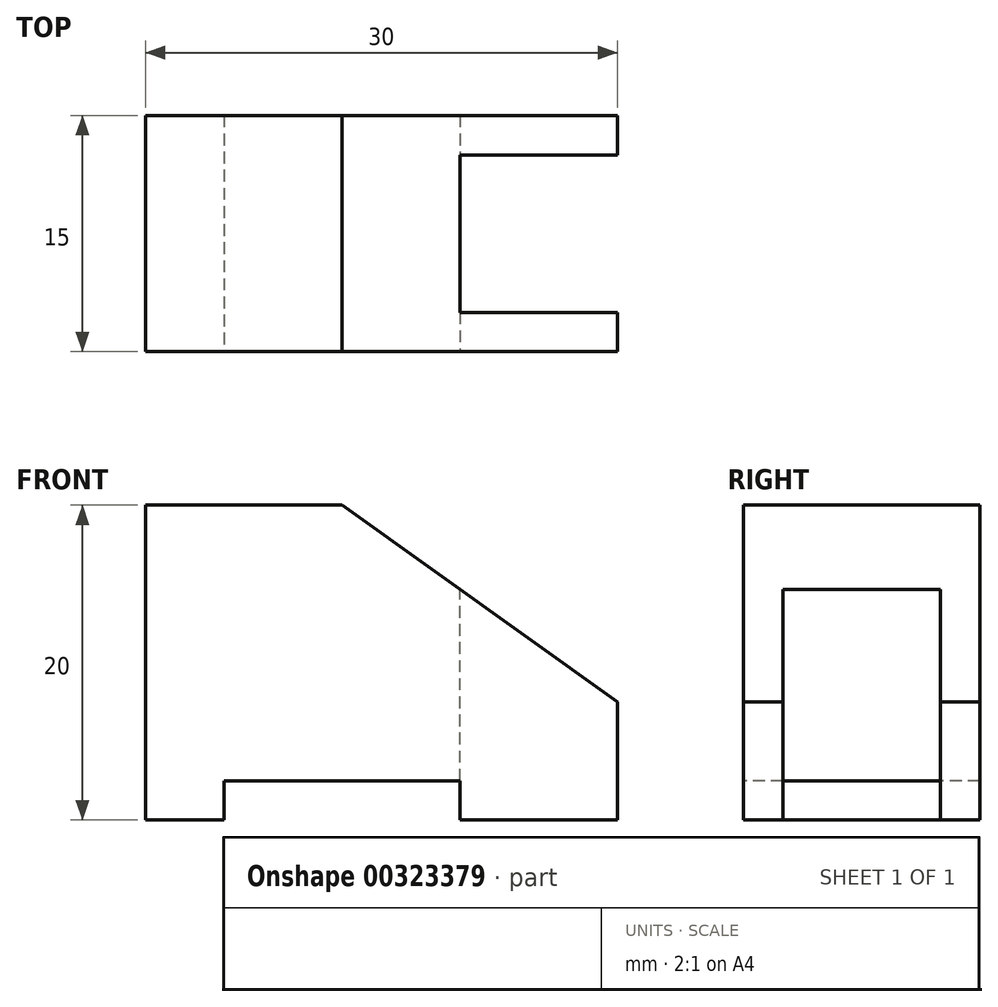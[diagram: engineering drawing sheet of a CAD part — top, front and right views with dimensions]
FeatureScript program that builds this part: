
annotation { "Feature Type Name" : "Feature", "Feature Type Description" : "" }
export const myFeature = defineFeature(function(context is Context, id is Id, definition is map)
    precondition{}
    {
        {
            var Q0;
            Q0=qCreatedBy(makeId("Front.planeOp"),FACE);
            var sketch = newSketch(context, id + "F0", { "sketchPlane" : qUnion([Q0])});
            skLineSegment(sketch, "E0", {"start": v(0, 0) * mm, "end": v(0, 20) * mm});
            skLineSegment(sketch, "E1", {"start": v(0, 20) * mm, "end": v(12.5, 20) * mm});
            skLineSegment(sketch, "E2", {"start": v(12.5, 20) * mm, "end": v(30, 7.5) * mm});
            skLineSegment(sketch, "E3", {"start": v(30, 7.5) * mm, "end": v(30, 0) * mm});
            skLineSegment(sketch, "E4", {"start": v(30, 0) * mm, "end": v(20, 0) * mm});
            skLineSegment(sketch, "E5", {"start": v(20, 0) * mm, "end": v(20, 2.5) * mm});
            skLineSegment(sketch, "E6", {"start": v(20, 2.5) * mm, "end": v(5, 2.5) * mm});
            skLineSegment(sketch, "E7", {"start": v(5, 2.5) * mm, "end": v(5, 0) * mm});
            skLineSegment(sketch, "E8", {"start": v(5, 0) * mm, "end": v(0, 0) * mm});
            skSolve(sketch);
        }
        {
            var Q0;
            Q0 = qSketchRegion(id + "F0", true);
            extrude(context, id + "F1", {"entities" : qUnion([Q0]), "oppositeDirection" : true, "depth" : 15 * mm});
        }
        {
            var Q0;
            Q0=makeQuery(id+"F1.opExtrude","SWEPT_FACE",FACE,{"disambiguationData":[OSD([sQuery(id+"F0.wireOp",EDGE,"E3")])]});
            var sketch = newSketch(context, id + "F2", { "sketchPlane" : qUnion([Q0])});
            skLineSegment(sketch, "E9", {"start": v(0, 0) * mm, "end": v(2.5, 0) * mm});
            skLineSegment(sketch, "E10", {"start": v(15, 0) * mm, "end": v(12.5, 0) * mm});
            skLineSegment(sketch, "E11.bottom", {"start": v(2.5, 0) * mm, "end": v(12.5, 0) * mm});
            skLineSegment(sketch, "E11.top", {"start": v(2.5, 15) * mm, "end": v(12.5, 15) * mm});
            skLineSegment(sketch, "E11.left", {"start": v(2.5, 0) * mm, "end": v(2.5, 15) * mm});
            skLineSegment(sketch, "E11.right", {"start": v(12.5, 0) * mm, "end": v(12.5, 15) * mm});
            skSolve(sketch);
        }
        {
            var Q0;
            Q0 = qSketchRegion(id + "F2", true);
            extrude(context, id + "F3", {"entities" : qUnion([Q0]), "operationType" : NewBodyOperationType.REMOVE, "oppositeDirection" : true, "depth" : 10 * mm});
        }
    });
